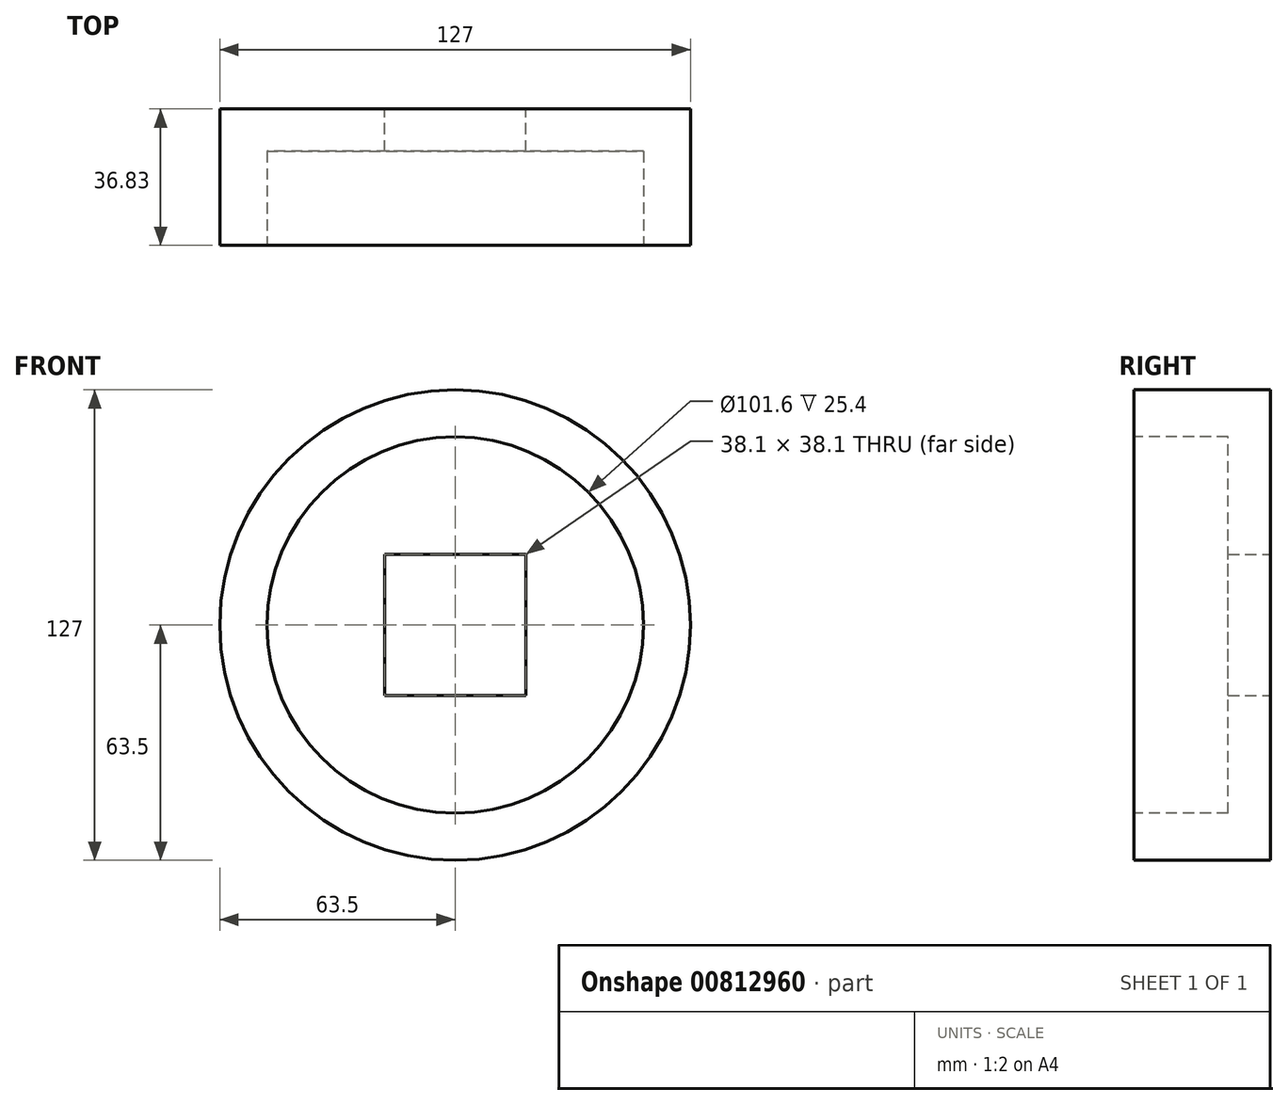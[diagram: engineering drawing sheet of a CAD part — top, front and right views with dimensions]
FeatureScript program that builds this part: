
annotation { "Feature Type Name" : "Feature", "Feature Type Description" : "" }
export const myFeature = defineFeature(function(context is Context, id is Id, definition is map)
    precondition{}
    {
        {
            var Q0;
            Q0=qCreatedBy(makeId("Front.planeOp"),FACE);
            var sketch = newSketch(context, id + "F0", { "sketchPlane" : qUnion([Q0])});
            skCircle(sketch, "E0", {"center": v(0, 0) * mm, "radius": 63.5 * mm});
            skSolve(sketch);
        }
        {
            var Q0;
            Q0 = qSketchRegion(id + "F0", true);
            extrude(context, id + "F1", {"entities" : qUnion([Q0]), "depth" : 36.83 * mm, "offsetDistance" : 25.4 * mm});
        }
        {
            var Q0;
            Q0=makeQuery(id+"F1.opExtrude","CAP_FACE",FACE,{"disambiguationData":[OSD([sQuery(id+"F0.wireOp",EDGE,"E0")])],"isStart":false});
            var sketch = newSketch(context, id + "F2", { "sketchPlane" : qUnion([Q0])});
            skCircle(sketch, "E1", {"center": v(0, 0) * mm, "radius": 50.8 * mm});
            skSolve(sketch);
        }
        {
            var Q0;
            Q0 = qSketchRegion(id + "F2", true);
            extrude(context, id + "F3", {"entities" : qUnion([Q0]), "operationType" : NewBodyOperationType.REMOVE, "oppositeDirection" : true, "depth" : 25.4 * mm, "offsetDistance" : 25.4 * mm});
        }
        {
            var Q0;
            Q0=makeQuery(id+"F1.opExtrude","CAP_FACE",FACE,{"disambiguationData":[OSD([sQuery(id+"F0.wireOp",EDGE,"E0")])],"isStart":true});
            var sketch = newSketch(context, id + "F4", { "sketchPlane" : qUnion([Q0])});
            skLineSegment(sketch, "E2.bottom", {"start": v(19.05, 19.05) * mm, "end": v(-19.05, 19.05) * mm});
            skLineSegment(sketch, "E2.top", {"start": v(19.05, -19.05) * mm, "end": v(-19.05, -19.05) * mm});
            skLineSegment(sketch, "E2.left", {"start": v(19.05, 19.05) * mm, "end": v(19.05, -19.05) * mm});
            skLineSegment(sketch, "E2.right", {"start": v(-19.05, 19.05) * mm, "end": v(-19.05, -19.05) * mm});
            skPoint(sketch, "E2.middle", {"position": v(0, 0) * mm});
            skSolve(sketch);
        }
        {
            var Q0;
            Q0 = qSketchRegion(id + "F4", true);
            extrude(context, id + "F5", {"entities" : qUnion([Q0]), "operationType" : NewBodyOperationType.REMOVE, "oppositeDirection" : true, "depth" : 25.4 * mm, "offsetDistance" : 25.4 * mm});
        }
    });
